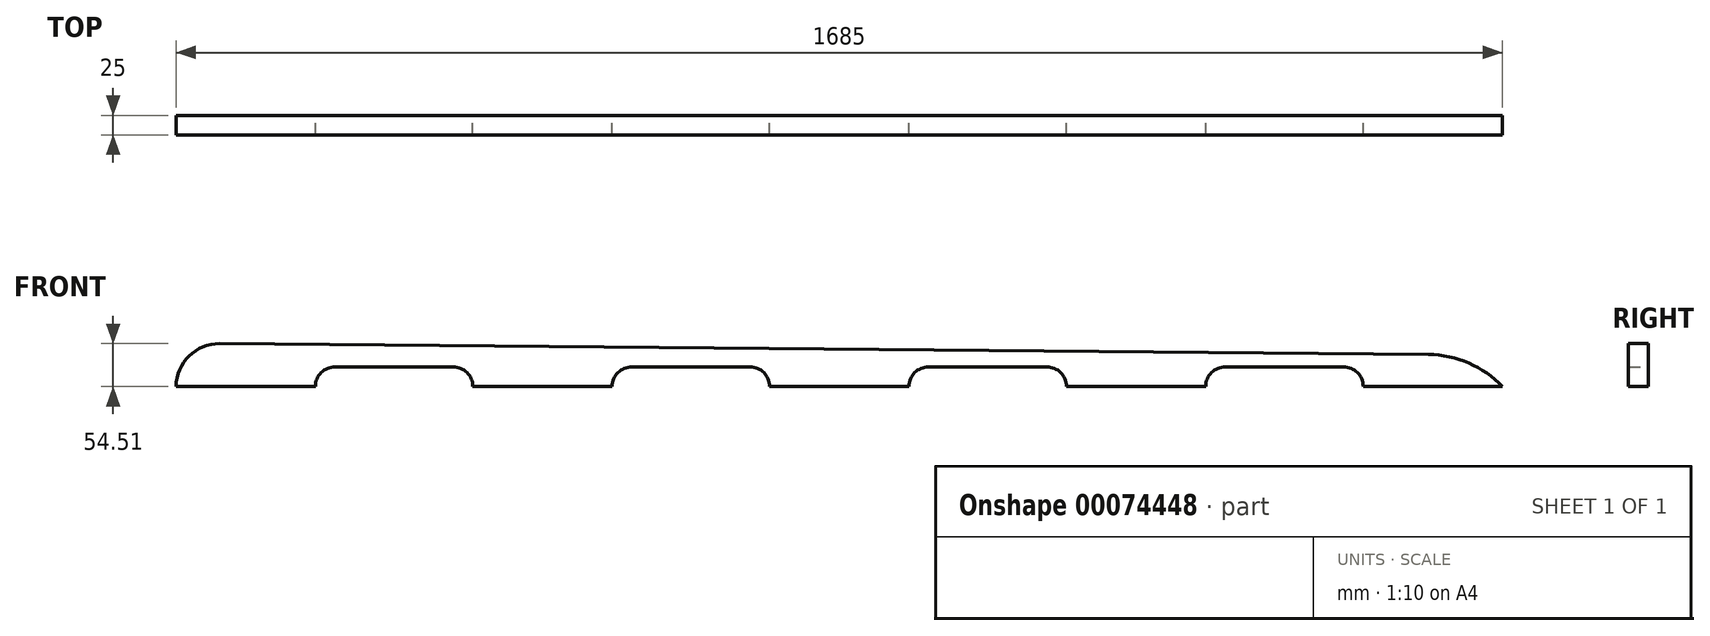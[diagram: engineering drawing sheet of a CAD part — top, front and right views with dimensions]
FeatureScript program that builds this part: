
annotation { "Feature Type Name" : "Feature", "Feature Type Description" : "" }
export const myFeature = defineFeature(function(context is Context, id is Id, definition is map)
    precondition{}
    {
        {
            var Q0;
            Q0=qCreatedBy(makeId("Front.planeOp"),FACE);
            var sketch = newSketch(context, id + "F0", { "sketchPlane" : qUnion([Q0])});
            skLineSegment(sketch, "E0", {"start": v(0, -0.5) * mm, "end": v(0, 0) * mm});
            skLineSegment(sketch, "E1", {"start": v(55.49, 54.5) * mm, "end": v(1685, 40) * mm});
            skLineSegment(sketch, "E2", {"start": v(1685, 40) * mm, "end": v(1685, 0) * mm});
            skLineSegment(sketch, "E3", {"start": v(1685, 0) * mm, "end": v(0, 0) * mm});
            skLineSegment(sketch, "E4.bottom", {"start": v(177, 0) * mm, "end": v(377, 0) * mm});
            skLineSegment(sketch, "E4.top", {"start": v(177, 25) * mm, "end": v(377, 25) * mm});
            skLineSegment(sketch, "E4.left", {"start": v(177, 0) * mm, "end": v(177, 25) * mm});
            skLineSegment(sketch, "E4.right", {"start": v(377, 0) * mm, "end": v(377, 25) * mm});
            skLineSegment(sketch, "E5.bottom", {"start": v(554, 0) * mm, "end": v(754, 0) * mm});
            skLineSegment(sketch, "E5.top", {"start": v(554, 25) * mm, "end": v(754, 25) * mm});
            skLineSegment(sketch, "E5.left", {"start": v(554, 0) * mm, "end": v(554, 25) * mm});
            skLineSegment(sketch, "E5.right", {"start": v(754, 0) * mm, "end": v(754, 25) * mm});
            skLineSegment(sketch, "E6.bottom", {"start": v(931, 0) * mm, "end": v(1131, 0) * mm});
            skLineSegment(sketch, "E6.top", {"start": v(931, 25) * mm, "end": v(1131, 25) * mm});
            skLineSegment(sketch, "E6.left", {"start": v(931, 0) * mm, "end": v(931, 25) * mm});
            skLineSegment(sketch, "E6.right", {"start": v(1131, 0) * mm, "end": v(1131, 25) * mm});
            skLineSegment(sketch, "E7.bottom", {"start": v(1308, 0) * mm, "end": v(1508, 0) * mm});
            skLineSegment(sketch, "E7.top", {"start": v(1308, 25) * mm, "end": v(1508, 25) * mm});
            skLineSegment(sketch, "E7.left", {"start": v(1308, 0) * mm, "end": v(1308, 25) * mm});
            skLineSegment(sketch, "E7.right", {"start": v(1508, 0) * mm, "end": v(1508, 25) * mm});
            skArc(sketch, "E8", {"start": v(1685, 0) * mm, "mid": v(1642.07, 29.74) * mm, "end": v(1591.04, 40.84) * mm});
            skPoint(sketch, "E9.visualSharp", {"position": v(0, 55) * mm});
            skArc(sketch, "E9.filletArc", {"start": v(55.49, 54.5) * mm, "mid": v(16.28, 38.57) * mm, "end": v(0, -0.5) * mm});
            skSolve(sketch);
        }
        {
            var Q0;
            Q0=makeQuery(id+"F0.imprint","IMPRINT",FACE,{"disambiguationData":[TD([[makeQuery(id+"F0.imprint","IMPRINT",EDGE,{"derivedFrom":sQuery(id+"F0.wireOp",EDGE,"E4.top")}),1.0]])]});
            extrude(context, id + "F1", {"entities" : qUnion([Q0]), "depth" : 25 * mm});
        }
        {
            var Q0;
            Q0=makeQuery(id+"F1.opExtrude","SWEPT_EDGE",EDGE,{"disambiguationData":[OSD([sQuery(id+"F0.wireOp",EDGE,"E4.top"),sQuery(id+"F0.wireOp",EDGE,"E4.left")])]});
            fillet(context, id + "F2", {"entities" : qUnion([Q0]), "radius" : 25 * mm, "tangentPropagation" : true, "allowEdgeOverflow" : false});
        }
        {
            var Q0;
            Q0=makeQuery(id+"F1.opExtrude","SWEPT_EDGE",EDGE,{"disambiguationData":[OSD([sQuery(id+"F0.wireOp",EDGE,"E4.top"),sQuery(id+"F0.wireOp",EDGE,"E4.right")])]});
            fillet(context, id + "F3", {"entities" : qUnion([Q0]), "radius" : 25 * mm, "tangentPropagation" : true, "allowEdgeOverflow" : false});
        }
        {
            var Q0;
            Q0=makeQuery(id+"F1.opExtrude","SWEPT_EDGE",EDGE,{"disambiguationData":[OSD([sQuery(id+"F0.wireOp",EDGE,"E5.top"),sQuery(id+"F0.wireOp",EDGE,"E5.right")])]});
            var Q1;
            Q1=makeQuery(id+"F1.opExtrude","SWEPT_EDGE",EDGE,{"disambiguationData":[OSD([sQuery(id+"F0.wireOp",EDGE,"E6.top"),sQuery(id+"F0.wireOp",EDGE,"E6.right")])]});
            fillet(context, id + "F4", {"entities" : qUnion([Q0, Q1]), "radius" : 25 * mm, "tangentPropagation" : true, "allowEdgeOverflow" : false});
        }
        {
            var Q0;
            Q0=makeQuery(id+"F1.opExtrude","SWEPT_EDGE",EDGE,{"disambiguationData":[OSD([sQuery(id+"F0.wireOp",EDGE,"E7.top"),sQuery(id+"F0.wireOp",EDGE,"E7.right")])]});
            var Q1;
            Q1=makeQuery(id+"F1.opExtrude","SWEPT_EDGE",EDGE,{"disambiguationData":[OSD([sQuery(id+"F0.wireOp",EDGE,"E5.top"),sQuery(id+"F0.wireOp",EDGE,"E5.left")])]});
            var Q2;
            Q2=makeQuery(id+"F1.opExtrude","SWEPT_EDGE",EDGE,{"disambiguationData":[OSD([sQuery(id+"F0.wireOp",EDGE,"E6.top"),sQuery(id+"F0.wireOp",EDGE,"E6.left")])]});
            var Q3;
            Q3=makeQuery(id+"F1.opExtrude","SWEPT_EDGE",EDGE,{"disambiguationData":[OSD([sQuery(id+"F0.wireOp",EDGE,"E7.top"),sQuery(id+"F0.wireOp",EDGE,"E7.left")])]});
            fillet(context, id + "F5", {"entities" : qUnion([Q0, Q1, Q2, Q3]), "radius" : 25 * mm, "tangentPropagation" : true, "allowEdgeOverflow" : false});
        }
    });
